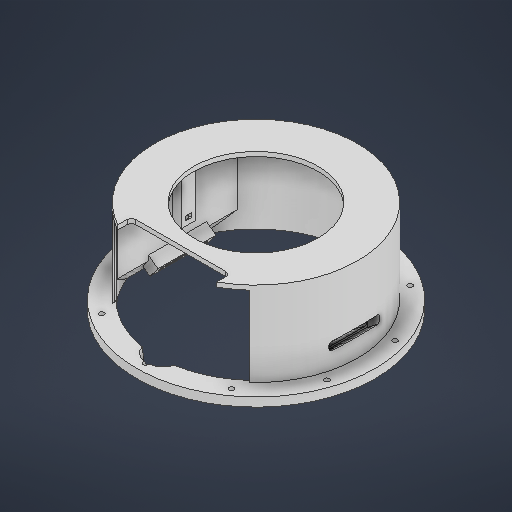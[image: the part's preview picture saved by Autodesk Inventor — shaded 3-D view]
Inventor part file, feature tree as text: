
AUTODESK INVENTOR PART (.ipt)
format: ipt  version: 2025 (Build 290162000, 162)  size: 521,728 bytes
history: native  units: in
note: dims shown in document units (in); Inventor stores cm internally (conversion verified against a paired STEP export)
features: extrude x17, sketch x15, plane x3, fillet x1, chamfer x1
ambient origin geometry x8: Origin, YZ Plane, XZ Plane, XY Plane, X Axis, Y Axis, Z Axis, Center Point
bodies: Solid1 (feature_tree)
feature tree (37):
  sketch  "Sketch1"  dims[d5=0.0in d7=0.0in]
  extrude  "Extrusion1"  TaperAngle=0.0deg  [1 undecoded]
  extrude  "Extrusion2"  Depth=4.5276in
  extrude  "Extrusion7"  Depth=0.2165in
  extrude  "Extrusion34"  Depth=6.1024in
  sketch  "Sketch30"  dims[d272=3.937in d273=4.1535in d274=0.0in d285=3.937in]
  plane  "Work Plane19"
  plane  "Work Plane21"
  plane  "Work Plane22"
  extrude  "Extrusion36"  Depth=4.1535in TaperAngle=0.0deg
  fillet  "Fillet19"  Radius=3.937in
  extrude  "Extrusion37"  Depth=2.0812in TaperAngle=0.0deg
  extrude  "Extrusion38"  Depth=0.1969in
  sketch  "Sketch35"  dims[d293=0.1969in d294=0.1969in]
  extrude  "Extrusion40"  Depth=1.5748in
  extrude  "Extrusion41"  Depth=0.1969in
  extrude  "Extrusion42"  Depth=0.3937in TaperAngle=0.0deg
  extrude  "Extrusion43"  Depth=1.7717in TaperAngle=0.0deg
  chamfer  "Chamfer14"  Distance=0.5906in
  sketch  "Sketch38"  dims[d301=2.9528in]
  extrude  "Extrusion44"  Depth=0.0689in
  extrude  "Extrusion45"  Depth=0.0689in TaperAngle=0.0deg
  sketch  "Sketch39"  dims[d308=6.378in]
  extrude  "Extrusion46"  Depth=0.0689in TaperAngle=0.0deg
  extrude  "Extrusion47"  Depth=0.0689in TaperAngle=0.0deg
  sketch  "Sketch43"  dims[d312=6.8898in d313=5.5413in d314=0.2362in d315=0.1969in d316=0.0in d317=0.1969in d318=0.0in d319=1.378in d320=0.0in d321=0.5906in d322=0.7874in d323=45.0deg d324=1.0in d326=0.315in d328=0.0in d329=0.0in d330=0.1772in d331=0.315in d332=0.0in d333=1.0in d334=0.2953in d335=0.1772in d336=0.0in d337=0.0in d338=0.315in d339=0.0in d340=0.8661in d341=0.8661in d344=0.5906in d345=0.5906in d346=0.5906in d347=0.5906in d348=0.3937in d349=0.0in d350=0.1969in d351=0.0in d352=0.5906in d353=0.5906in d354=0.5906in d355=0.5906in d356=0.3937in d357=0.1969in d358=0.0in d359=0.0in d360=0.0in d361=0.0689in d113=0.0197in d114=0.0344in d115=0.0197in d116=0.0344in d167=0.0197in d168=0.0344in d169=0.0197in d170=0.0344in d215=0.0197in d216=0.0344in d217=0.0197in d218=0.0344in d219=0.0in d220=0.0in d254=0.0197in d255=0.0344in d256=0.0197in d257=0.0344in]
  extrude  "Extrusion49"  Depth=0.5906in TaperAngle=45.0deg
  extrude  "Extrusion50"  Depth=0.0689in
  sketch  "Sketch2"  dims[d18=0.0in d52=4.5276in]
  sketch  "Sketch Circular Pattern5"  dims[d264=9.8425in d265=0.2165in]
  sketch  "Sketch28"  dims[d266=3.937in d268=360.0deg d271=6.1024in]
  sketch  "Sketch31"  dims[d286=1.5748in d287=2.0812in d288=0.0in]
  sketch  "Sketch32"  dims[d289=3.5039in d290=0.1969in]
  sketch  "Sketch33"  dims[d291=4.4094in d292=1.5748in]
  sketch  "Sketch36"  dims[d295=3.3465in d296=0.3937in d297=0.0in]
  sketch  "Sketch37"  dims[d298=0.6299in d299=1.7717in d300=0.0in]
  sketch  "Sketch42"  dims[d309=0.2805in d310=0.5906in d311=0.0in]
note: 1 required parameter value undecoded (feature->parameter linkage not recoverable at this tier; creation-order binding heuristic only, values carry confidence <= 0.55)
